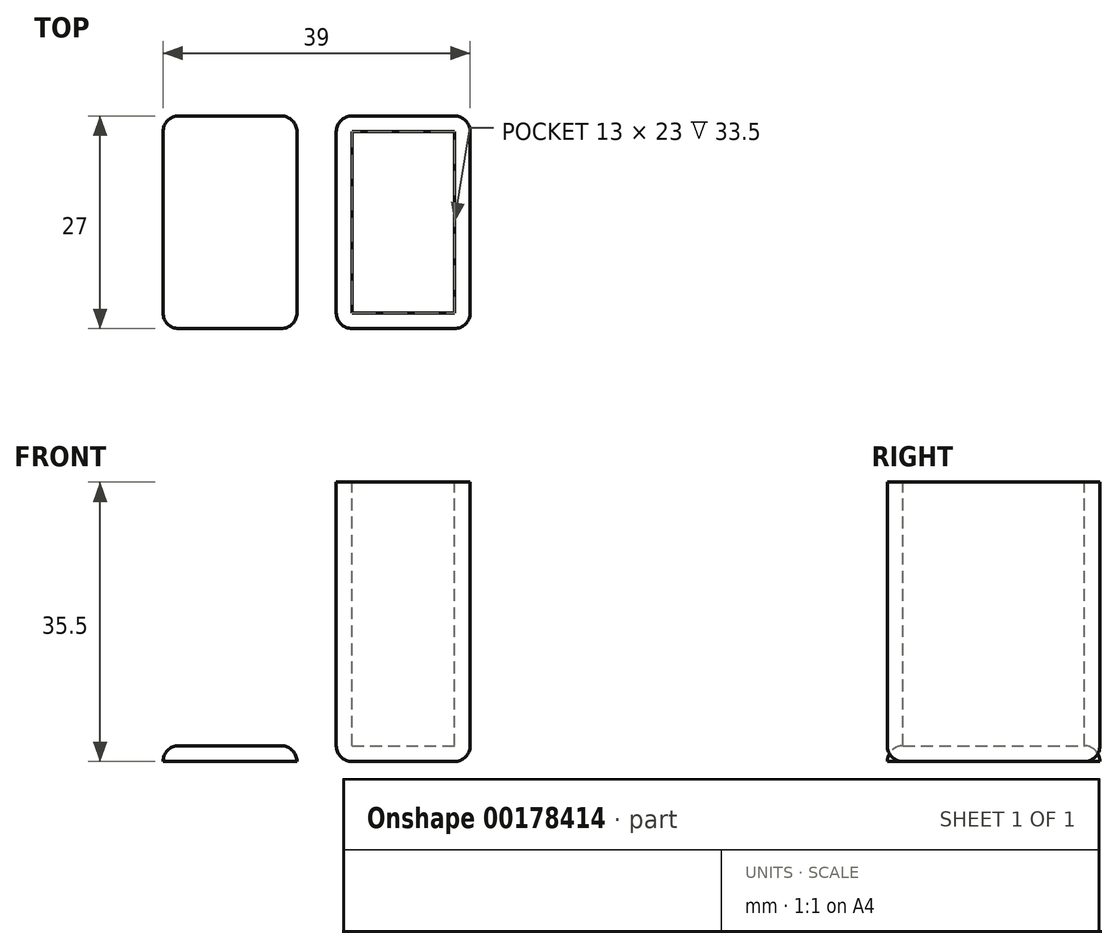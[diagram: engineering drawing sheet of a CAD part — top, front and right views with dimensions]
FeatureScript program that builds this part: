
annotation { "Feature Type Name" : "Feature", "Feature Type Description" : "" }
export const myFeature = defineFeature(function(context is Context, id is Id, definition is map)
    precondition{}
    {
        {
            var Q0;
            Q0=qCreatedBy(makeId("Top.planeOp"),FACE);
            var sketch = newSketch(context, id + "F0", { "sketchPlane" : qUnion([Q0])});
            skLineSegment(sketch, "E0.bottom", {"start": v(0, 0) * mm, "end": v(17, 0) * mm});
            skLineSegment(sketch, "E0.top", {"start": v(0, 27) * mm, "end": v(17, 27) * mm});
            skLineSegment(sketch, "E0.left", {"start": v(0, 0) * mm, "end": v(0, 27) * mm});
            skLineSegment(sketch, "E0.right", {"start": v(17, 0) * mm, "end": v(17, 27) * mm});
            skSolve(sketch);
        }
        {
            var Q0;
            Q0=makeQuery(id+"F0.imprint","IMPRINT",FACE,{"disambiguationData":[TD([[makeQuery(id+"F0.imprint","IMPRINT",EDGE,{"derivedFrom":sQuery(id+"F0.wireOp",EDGE,"E0.bottom")}),1.0]])]});
            extrude(context, id + "F1", {"entities" : qUnion([Q0]), "depth" : 35.5 * mm});
        }
        {
            var Q0;
            Q0=makeQuery(id+"F1.opExtrude","CAP_FACE",FACE,{"disambiguationData":[OSD([sQuery(id+"F0.wireOp",EDGE,"E0.bottom"),sQuery(id+"F0.wireOp",EDGE,"E0.top"),sQuery(id+"F0.wireOp",EDGE,"E0.left"),sQuery(id+"F0.wireOp",EDGE,"E0.right")])],"isStart":false});
            var sketch = newSketch(context, id + "F2", { "sketchPlane" : qUnion([Q0])});
            skLineSegment(sketch, "E1.bottom", {"start": v(0, 0) * mm, "end": v(2, 0) * mm, "construction": true});
            skLineSegment(sketch, "E1.top", {"start": v(0, 2) * mm, "end": v(2, 2) * mm, "construction": true});
            skLineSegment(sketch, "E1.left", {"start": v(0, 0) * mm, "end": v(0, 2) * mm, "construction": true});
            skLineSegment(sketch, "E1.right", {"start": v(2, 0) * mm, "end": v(2, 2) * mm, "construction": true});
            skLineSegment(sketch, "E2.bottom", {"start": v(2, 2) * mm, "end": v(15, 2) * mm});
            skLineSegment(sketch, "E2.top", {"start": v(2, 25) * mm, "end": v(15, 25) * mm});
            skLineSegment(sketch, "E2.left", {"start": v(2, 2) * mm, "end": v(2, 25) * mm});
            skLineSegment(sketch, "E2.right", {"start": v(15, 2) * mm, "end": v(15, 25) * mm});
            skSolve(sketch);
        }
        {
            var Q0;
            Q0 = qSketchRegion(id + "F2", true);
            extrude(context, id + "F3", {"entities" : qUnion([Q0]), "operationType" : NewBodyOperationType.REMOVE, "oppositeDirection" : true, "depth" : 33.5 * mm});
        }
        {
            var Q0;
            Q0=makeQuery(id+"F1.opExtrude","CAP_FACE",FACE,{"disambiguationData":[OSD([sQuery(id+"F0.wireOp",EDGE,"E0.bottom"),sQuery(id+"F0.wireOp",EDGE,"E0.top"),sQuery(id+"F0.wireOp",EDGE,"E0.left"),sQuery(id+"F0.wireOp",EDGE,"E0.right")])],"isStart":true});
            var Q1;
            Q1=makeQuery(id+"F1.opExtrude","SWEPT_EDGE",EDGE,{"disambiguationData":[OSD([sQuery(id+"F0.wireOp",EDGE,"E0.bottom"),sQuery(id+"F0.wireOp",EDGE,"E0.right")])]});
            var Q2;
            Q2=makeQuery(id+"F1.opExtrude","SWEPT_EDGE",EDGE,{"disambiguationData":[OSD([sQuery(id+"F0.wireOp",EDGE,"E0.bottom"),sQuery(id+"F0.wireOp",EDGE,"E0.left")])]});
            var Q3;
            Q3=makeQuery(id+"F1.opExtrude","SWEPT_EDGE",EDGE,{"disambiguationData":[OSD([sQuery(id+"F0.wireOp",EDGE,"E0.top"),sQuery(id+"F0.wireOp",EDGE,"E0.right")])]});
            var Q4;
            Q4=makeQuery(id+"F1.opExtrude","SWEPT_EDGE",EDGE,{"disambiguationData":[OSD([sQuery(id+"F0.wireOp",EDGE,"E0.top"),sQuery(id+"F0.wireOp",EDGE,"E0.left")])]});
            fillet(context, id + "F4", {"entities" : qUnion([Q0, Q1, Q2, Q3, Q4]), "radius" : 2 * mm, "tangentPropagation" : true, "allowEdgeOverflow" : false});
        }
        {
            var Q0;
            Q0=qCreatedBy(makeId("Top.planeOp"),FACE);
            var sketch = newSketch(context, id + "F5", { "sketchPlane" : qUnion([Q0])});
            skLineSegment(sketch, "E3", {"start": v(0, 0) * mm, "end": v(-5, 0) * mm, "construction": true});
            skLineSegment(sketch, "E4.bottom", {"start": v(-7, 0) * mm, "end": v(-20, 0) * mm});
            skLineSegment(sketch, "E4.top", {"start": v(-7, 27) * mm, "end": v(-20, 27) * mm});
            skLineSegment(sketch, "E4.left", {"start": v(-5, 2) * mm, "end": v(-5, 25) * mm});
            skLineSegment(sketch, "E4.right", {"start": v(-22, 2) * mm, "end": v(-22, 25) * mm});
            skPoint(sketch, "E5.visualSharp", {"position": v(-22, 27) * mm});
            skArc(sketch, "E5.filletArc", {"start": v(-20, 27) * mm, "mid": v(-21.41, 26.41) * mm, "end": v(-22, 25) * mm});
            skPoint(sketch, "E6.visualSharp", {"position": v(-22, 0) * mm});
            skArc(sketch, "E6.filletArc", {"start": v(-22, 2) * mm, "mid": v(-21.41, 0.59) * mm, "end": v(-20, 0) * mm});
            skPoint(sketch, "E7.visualSharp", {"position": v(-5, 0) * mm});
            skArc(sketch, "E7.filletArc", {"start": v(-7, 0) * mm, "mid": v(-5.59, 0.59) * mm, "end": v(-5, 2) * mm});
            skPoint(sketch, "E8.visualSharp", {"position": v(-5, 27) * mm});
            skArc(sketch, "E8.filletArc", {"start": v(-5, 25) * mm, "mid": v(-5.59, 26.41) * mm, "end": v(-7, 27) * mm});
            skSolve(sketch);
        }
        {
            var Q0;
            Q0 = qSketchRegion(id + "F5", true);
            extrude(context, id + "F6", {"entities" : qUnion([Q0]), "depth" : 2 * mm});
        }
        {
            var Q0;
            Q0=makeQuery(id+"F6.opExtrude","CAP_FACE",FACE,{"disambiguationData":[OSD([sQuery(id+"F5.wireOp",EDGE,"E4.bottom"),sQuery(id+"F5.wireOp",EDGE,"E4.top"),sQuery(id+"F5.wireOp",EDGE,"E4.left"),sQuery(id+"F5.wireOp",EDGE,"E4.right"),sQuery(id+"F5.wireOp",EDGE,"E5.filletArc"),sQuery(id+"F5.wireOp",EDGE,"E6.filletArc"),sQuery(id+"F5.wireOp",EDGE,"E7.filletArc"),sQuery(id+"F5.wireOp",EDGE,"E8.filletArc")])],"isStart":false});
            fillet(context, id + "F7", {"entities" : qUnion([Q0]), "radius" : 2 * mm, "tangentPropagation" : true, "allowEdgeOverflow" : false});
        }
    });
